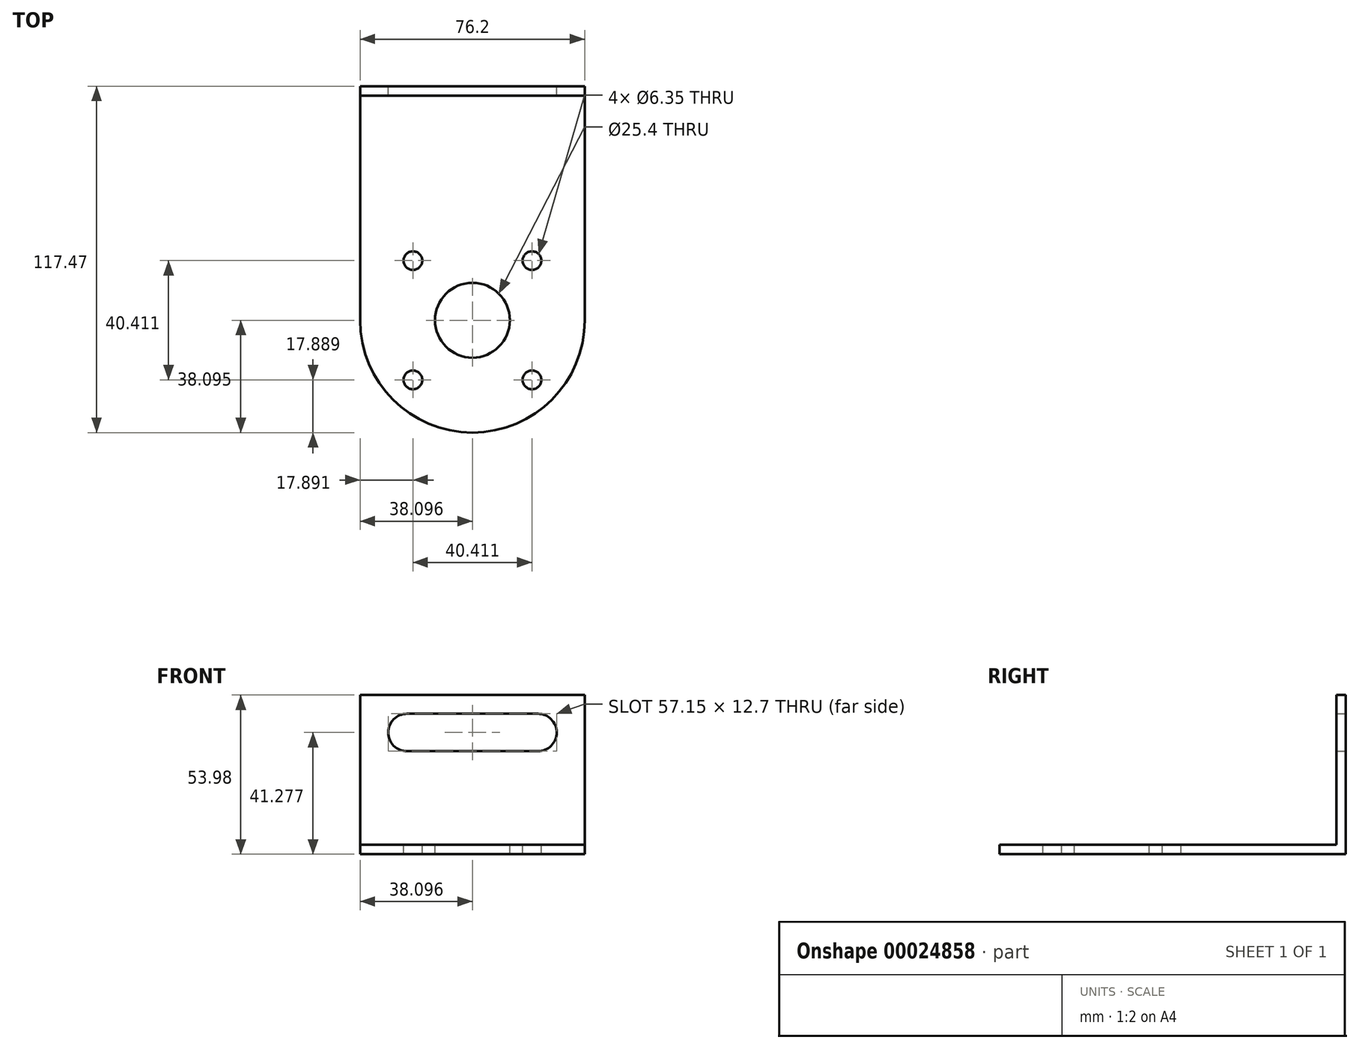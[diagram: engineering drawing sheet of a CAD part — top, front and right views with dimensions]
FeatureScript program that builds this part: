
annotation { "Feature Type Name" : "Feature", "Feature Type Description" : "" }
export const myFeature = defineFeature(function(context is Context, id is Id, definition is map)
    precondition{}
    {
        {
            var Q0;
            Q0=qCreatedBy(makeId("Front.planeOp"),FACE);
            var sketch = newSketch(context, id + "F0", { "sketchPlane" : qUnion([Q0])});
            skLineSegment(sketch, "E0", {"start": v(-71.84, 41.78) * mm, "end": v(4.36, 41.78) * mm});
            skLineSegment(sketch, "E1", {"start": v(4.36, 41.78) * mm, "end": v(4.36, -12.2) * mm});
            skLineSegment(sketch, "E2", {"start": v(4.36, -12.2) * mm, "end": v(-71.84, -12.2) * mm});
            skLineSegment(sketch, "E3", {"start": v(-71.84, -12.2) * mm, "end": v(-71.84, 41.78) * mm});
            skLineSegment(sketch, "E4", {"start": v(-55.97, 41.78) * mm, "end": v(-55.97, 35.43) * mm, "construction": true});
            skLineSegment(sketch, "E5", {"start": v(-11.52, 41.78) * mm, "end": v(-11.52, -12.2) * mm, "construction": true});
            skLineSegment(sketch, "E6", {"start": v(-71.84, 29.08) * mm, "end": v(4.36, 29.08) * mm, "construction": true});
            skArc(sketch, "E7", {"start": v(-55.97, 35.43) * mm, "mid": v(-62.32, 29.08) * mm, "end": v(-55.97, 22.73) * mm});
            skArc(sketch, "E8", {"start": v(-11.52, 22.73) * mm, "mid": v(-5.17, 29.08) * mm, "end": v(-11.52, 35.43) * mm});
            skLineSegment(sketch, "E9", {"start": v(-55.97, 35.43) * mm, "end": v(-11.52, 35.43) * mm});
            skLineSegment(sketch, "E10", {"start": v(-55.97, 22.73) * mm, "end": v(-11.52, 22.73) * mm});
            skLineSegment(sketch, "E11.trimOffspring", {"start": v(-55.97, 22.73) * mm, "end": v(-55.97, -12.2) * mm, "construction": true});
            skSolve(sketch);
        }
        {
            var Q0;
            Q0=makeQuery(id+"F0.imprint","IMPRINT",FACE,{"disambiguationData":[TD([[makeQuery(id+"F0.imprint","IMPRINT",EDGE,{"derivedFrom":sQuery(id+"F0.wireOp",EDGE,"E0")}),-1.0]])]});
            extrude(context, id + "F1", {"entities" : qUnion([Q0]), "depth" : 3.17 * mm});
        }
        {
            var Q0;
            Q0=makeQuery(id+"F1.opExtrude","CAP_FACE",FACE,{"disambiguationData":[OSD([sQuery(id+"F0.wireOp",EDGE,"E0"),sQuery(id+"F0.wireOp",EDGE,"E1"),sQuery(id+"F0.wireOp",EDGE,"E2"),sQuery(id+"F0.wireOp",EDGE,"E3"),sQuery(id+"F0.wireOp",EDGE,"E7"),sQuery(id+"F0.wireOp",EDGE,"E8"),sQuery(id+"F0.wireOp",EDGE,"E9"),sQuery(id+"F0.wireOp",EDGE,"E10")])],"isStart":false});
            var sketch = newSketch(context, id + "F2", { "sketchPlane" : qUnion([Q0])});
            skLineSegment(sketch, "E12", {"start": v(-71.84, -9.02) * mm, "end": v(4.36, -9.02) * mm});
            skSolve(sketch);
        }
        {
            var Q0;
            {var subQ1=sQuery(id+"F2.wireOp",EDGE,"E12");Q0=makeQuery(id+"F2.imprint","IMPRINT",FACE,{"disambiguationData":[TD([[makeQuery(id+"F2.imprint","IMPRINT",EDGE,{"derivedFrom":subQ1}),-1.0]])]});}
            extrude(context, id + "F3", {"entities" : qUnion([Q0]), "operationType" : NewBodyOperationType.ADD, "depth" : 76.2 * mm});
        }
        {
            var Q0;
            Q0=makeQuery(id+"F3.opExtrude","SWEPT_FACE",FACE,{"disambiguationData":[OSD([sQuery(id+"F2.wireOp",EDGE,"E12")])]});
            var sketch = newSketch(context, id + "F4", { "sketchPlane" : qUnion([Q0])});
            skCircle(sketch, "E13", {"center": v(-33.74, -79.38) * mm, "radius": 38.1 * mm});
            skSolve(sketch);
        }
        {
            var Q0;
            {var subQ0=sQuery(id+"F2.wireOp",EDGE,"E12");var subQ1=makeQuery(id+"F3.opExtrude","CAP_EDGE",EDGE,{"disambiguationData":[OSD([subQ0])],"isStart":false});Q0=makeQuery(id+"F4.imprint","IMPRINT",FACE,{"disambiguationData":[TD([[makeQuery(id+"F4.imprint","IMPRINT",EDGE,{"derivedFrom":subQ1}),-1.0]])]});}
            extrude(context, id + "F5", {"entities" : qUnion([Q0]), "operationType" : NewBodyOperationType.ADD, "oppositeDirection" : true, "depth" : 3.17 * mm});
        }
        {
            var Q0;
            {var subQ0=sQuery(id+"F2.wireOp",EDGE,"E12");Q0=makeQuery(id+"F5.boolean.opBoolean","MERGE",FACE,{"derivedFrom":[makeQuery(id+"F3.opExtrude","SWEPT_FACE",FACE,{"disambiguationData":[OSD([subQ0])]}),makeQuery(id+"F5.opExtrude","CAP_FACE",FACE,{"disambiguationData":[OSD([subQ0,sQuery(id+"F4.wireOp",EDGE,"E13")])],"isStart":true})]});}
            var sketch = newSketch(context, id + "F6", { "sketchPlane" : qUnion([Q0])});
            skLineSegment(sketch, "E14", {"start": v(-71.84, -79.38) * mm, "end": v(4.36, -79.38) * mm, "construction": true});
            skLineSegment(sketch, "E15", {"start": v(-33.74, -79.38) * mm, "end": v(-33.74, -117.47) * mm, "construction": true});
            skCircle(sketch, "E16", {"center": v(-33.74, -79.38) * mm, "radius": 12.7 * mm});
            skLineSegment(sketch, "E17", {"start": v(-33.74, -79.38) * mm, "end": v(-1.33, -111.79) * mm, "construction": true});
            skCircle(sketch, "E18", {"center": v(-33.74, -79.38) * mm, "radius": 28.58 * mm, "construction": true});
            skCircle(sketch, "E19", {"center": v(-13.54, -99.58) * mm, "radius": 3.18 * mm});
            skCircle(sketch, "E20.1.0", {"center": v(-13.54, -59.17) * mm, "radius": 3.18 * mm});
            skCircle(sketch, "E20.2.0", {"center": v(-53.95, -59.17) * mm, "radius": 3.18 * mm});
            skCircle(sketch, "E20.3.0", {"center": v(-53.95, -99.58) * mm, "radius": 3.18 * mm});
            skSolve(sketch);
        }
        {
            var Q0;
            Q0=makeQuery(id+"F6.imprint","IMPRINT",FACE,{"disambiguationData":[TD([[makeQuery(id+"F6.imprint","IMPRINT",EDGE,{"derivedFrom":sQuery(id+"F6.wireOp",EDGE,"E16")}),1.0]])]});
            var Q1;
            Q1=makeQuery(id+"F6.imprint","IMPRINT",FACE,{"disambiguationData":[TD([[makeQuery(id+"F6.imprint","IMPRINT",EDGE,{"derivedFrom":sQuery(id+"F6.wireOp",EDGE,"E20.1.0")}),1.0]])]});
            var Q2;
            Q2=makeQuery(id+"F6.imprint","IMPRINT",FACE,{"disambiguationData":[TD([[makeQuery(id+"F6.imprint","IMPRINT",EDGE,{"derivedFrom":sQuery(id+"F6.wireOp",EDGE,"E19")}),1.0]])]});
            var Q3;
            Q3=makeQuery(id+"F6.imprint","IMPRINT",FACE,{"disambiguationData":[TD([[makeQuery(id+"F6.imprint","IMPRINT",EDGE,{"derivedFrom":sQuery(id+"F6.wireOp",EDGE,"E20.2.0")}),1.0]])]});
            var Q4;
            Q4=makeQuery(id+"F6.imprint","IMPRINT",FACE,{"disambiguationData":[TD([[makeQuery(id+"F6.imprint","IMPRINT",EDGE,{"derivedFrom":sQuery(id+"F6.wireOp",EDGE,"E20.3.0")}),1.0]])]});
            extrude(context, id + "F7", {"entities" : qUnion([Q0, Q1, Q2, Q3, Q4]), "operationType" : NewBodyOperationType.REMOVE, "oppositeDirection" : true, "depth" : 25.4 * mm});
        }
    });
